# Revit family: Maxlogic Ручные извещатели пожарные
name_source: partatom
category: Fire Alarm Devices
units: mm (PartAtom-declared; Revit-internal decimal feet)

## family parameters
Cut with Voids When Loaded = No
Host = Face
Maintain Annotation Orientation = Yes
OmniClass Number = 23.85.30.21
OmniClass Title = Environmental Detection/Registration
Part Type = Normal
Room Calculation Point = No
Round Connector Dimension = Use Diameter
Shared = No

## types (3) — shared parameters
Manufacturer = Mavili Elektronik Ticaret A.Ş.
Model = MaxLogic
URL = https://www.mavili.com.tr
Адрес №1 = Şerifali Mahallesi Kutup Sokak No:27/1-2-4 Ümraniye TR-34775 İSTANBUL
Вторичный материал = Пластмассовый
Гарантийный срок = Года
Гарантийный срок запчастей = 2
Гарантия срока службы = 2
Главный Материал = Красный пластмассовый ABS
Инструкция по установке = https://mavilielektronik.com
Класс защиты = IP22D
Монтажная высота = Выше пола на 140 см (+/-200мм)
Монтажная поверхность = Настенная
Номер телефона = (+)90 216 466 45 05
Номер факса = (+)90 216 466 45 10
Номинальная высота = 91 мм
Номинальная глубина = 58 мм
Номинальная ширина = 87 мм
Прозрачная защитная крышка = ML-0710
Производительность кода = EN 54-11
Рабочая Температура = (-10°C) - (+55°C)
Рабочее напряжение (по умолчанию) = 24 В Пост. ток
Цвет = Красный
zero-valued in all types: Cost, Default Elevation

## per-type parameters (varying)
| type | Description | Вес | Диапазон рабочего напряжения | Код продукта | Настройка адреса устройства | Номер позы общественных работ | Светодиод кнопки |
| Maxlogic Неадресный пожарный ручной извещатель | Неадресный пожарный ручной извещатель | 140 гр | 10-30 В Пост. ток | ML-2710 |  | 830-102 | No |
| Maxlogic Адресный пожарный ручной извещатель | Адресный пожарный ручной извещатель | 150 гр | 18-33 В Пост. ток | ML-1710 | Модульная адресация | 833-557 | Yes |
| Maxlogic Адресный пожарный ручной извещатель, с изолятором КЗ | Адресный пожарный ручной извещатель, с изолятором КЗ | 150 гр | 10-30 В Пост. ток | ML-1710.SCI | Модульная адресация | 833-558 | Yes |

## geometry (parser evidence)
native form markers: Sweep x3
no freeform markers — native parametric forms only
